# Revit family: PRD_FrankeWS_UninterruptiblePowerSupplyUPSUnits_ZAQUA006
name_source: partatom
category: Electrical Equipment
revit_build: Autodesk Revit 2018 (Build: 20190510_1515(x64)
units: mm (PartAtom-declared; Revit-internal decimal feet)

## family parameters
Always vertical = Yes
Cut with Voids When Loaded = No
OmniClass Number = 23.45.55.11
OmniClass Title = Sanitary Components
Part Type = Transformer
Room Calculation Point = No
Round Connector Dimension = Use Diameter
Shared = No
Work Plane-Based = No

## types (1)
- ZAQUA006
    AssetType = Fixed
    BIMObjectName = PRD_AR_UninterruptiblePowerSupplyUPSUnits_ZAQUA006
    Category = Pr_60_70_64_93, Uninterruptible power supply (UPS) units
    Description = Uninterruptible power supply - A3000 open for connection to ECC function controller, 24 V DC / 3.2 Ah.
    DurationUnit = year
    GrossWeight = 3.76 kg
    IP_Code = IP20
    IfcExportAs = IfcTransformerType
    IfcExportType = NOTDEFINED
    Manufacturer = KWC Group AG
    ManufacturerName = KWC Group AG
    ManufacturerURL = www.kwc.com
    MaximumApparentPower = 0 VA
    Model = ZAQUA006
    ModelNumber = 2000100977
    ModelReference = ZAQUA006
    NBSDescription = Uninterruptible power supply (UPS) unit
    NBSReference = 90-60-40/410
    Name = Uninterruptible power supply ZAQUA006
    NetWeight = 3.42 kg
    NominalHeight = 162 mm  [stored 0.531496 ft]
    NominalLength = 152 mm  [stored 0.498688 ft]
    NominalWidth = 115 mm  [stored 0.377297 ft]
    PowerSupplyMaterial = <By Category>
    PrimaryApparentPower = 0 VA
    PrimaryCurrent = 0 A
    PrimaryFrequency = 50 Hz
    PrimaryVoltage = 230 V
    ProductInformation = https://pim.kwc.com
    SecondaryApparentPower = 0 VA
    SecondaryCurrent = 0 A
    SecondaryCurrentType = DC
    SecondaryFrequency = 0 Hz
    SecondaryVoltage = 24 V
    Size = 115 x 162 x 152 mm
    URL = www.kwc.com
    Uniclass2015Code = Pr_60_70_64_93
    Uniclass2015Title = Uninterruptible power supply (UPS) units
    Uniclass2015Version = Products v1.7
    Version = 1
    Voltage = 230
    WarrantyDurationUnit = year

note: [stored X ft] marks values corroborated as IEEE doubles in the binary element streams (Revit-internal decimal feet)

## geometry (parser evidence)
native form markers: Sweep x3
no freeform markers — native parametric forms only
